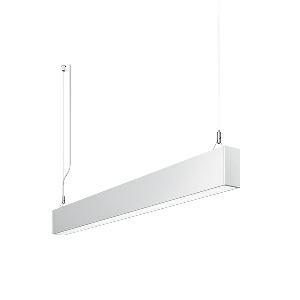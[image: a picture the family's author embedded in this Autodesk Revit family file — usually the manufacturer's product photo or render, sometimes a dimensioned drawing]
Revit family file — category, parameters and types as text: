
# Revit family: idoo_line_-_ilp_4000_830_d_00805735_cdef
name_source: partatom
category: Lighting Fixtures
units: mm (PartAtom-declared; Revit-internal decimal feet)

## family parameters
Cut with Voids When Loaded = No
Host = Face
Light Source = No
Part Type = Normal
Room Calculation Point = No
Round Connector Dimension = Use Diameter
Shared = No

## types (1)
- IDOO.line - ILP 4000/830/D (1 x LED, 3750 lm, 3000K)
    Apparent Load = 29 VA
    Approval mark = CE
    CIE Flux Codes = 66 91 98 40 100
    Color Rendering = 80-89
    Color Temperature = 3000K
    Control Gear = Electronic ballast
    Default Elevation = 1800 mm
    Description = ILP 4000/830/D|Suspended luminaire|light source: LED|connected load: 220-240V, 50/60Hz|Power consumption: approx. 29 W|standby: approx. 0,15|luminous flux: 3750 lm|luminous efficacy: 129 lm/W|light distribution: Direct/indirect|direct ratio: approx. 40 %|colour temperature: Warm white, ca. 3000 K|color rendering index (CRI): >= 80|chromaticity tolerance:  3 SDCM|System of protection: IP 40|technology: Continuously dimmable|luminaire body|material: Sectional aluminium|colour: White|lamp cover: Acrylic (PMMA), Clear|mains lead: 2.00 m With free stranded wires|Fastening: Steel cable 0.3 - 0.7 m|glare control: Prism aperture|luminance(L65): <= 2700 cd/m|unified glare rating(4H 8H): <=  16|special features: DALI Load 1x, TouchDIM - dimming via standard switch, Flicker-free, Suitable as emergency lighting|
    Frequency = 50 Hz
    Height = 110 mm
    Lamp = 1 x LED
    Lamp Light Flux = 3750 lm
    Lamp count = 1
    Length = 1414 mm
    Luminous efficacy = 129 lm/W
    Manufacturer = Waldmann
    ModVariant = No
    Model = 00805735
    Mounting Place = Ceiling
    Mounting Type = Pendant
    Number of Poles = 1
    OnlyDefault = Yes
    Power Factor = 1
    Product Name = IDOO.line - ILP 4000/830/D
    Product group = Suspended luminaire
    ProductGroupID = 9
    Protection Class = Protection class I
    Protection Degree = IP 40
    RLX_Detail_Level = 1
    RLX_Emergency_Light_Flux = 0 lm
    RLX_Emergency_Type = 0
    RLX_Emergency_Type_DB = No
    RlxData = <blob elided: 19473 chars, md5=4227c2f2>
    Socket = socket
    Standby Power = 0 W
    System Light Flux = 3750 lm
    System Power = 29 W
    Type Comments = Product without accessories
    Type Image = 113291000-00692522.jpg
    URL = http://relux.com
    VarID = ---
    Voltage = 230 V
    Voltage Range = 220-240 V
    Weight = 0.00 kg
    Width = 60 mm  [stored 0.19685 ft]

note: [stored X ft] marks values corroborated as IEEE doubles in the binary element streams (Revit-internal decimal feet)

## geometry (parser evidence)
native form markers: Blend x4, Sweep x14
no freeform markers — native parametric forms only
